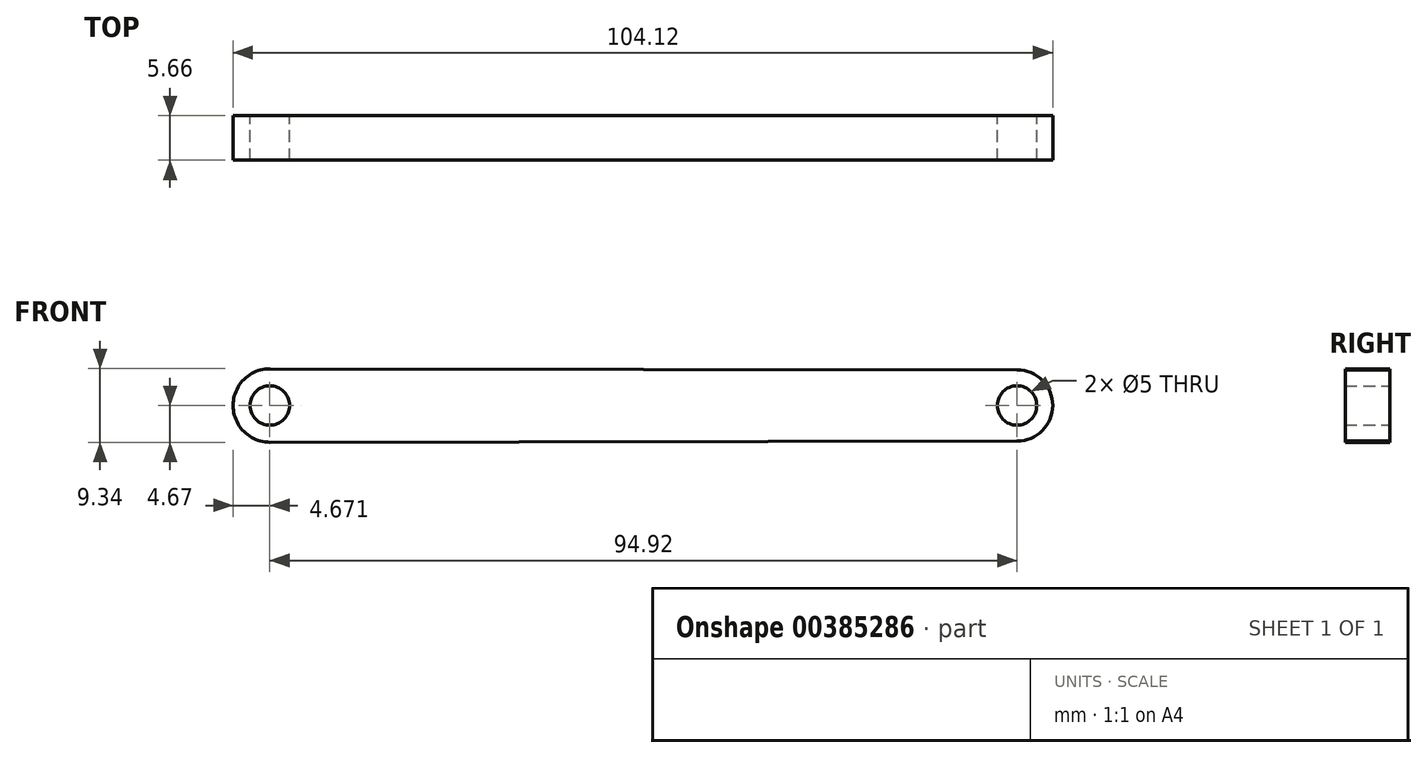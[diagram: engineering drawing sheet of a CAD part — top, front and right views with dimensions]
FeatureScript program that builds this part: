
annotation { "Feature Type Name" : "Feature", "Feature Type Description" : "" }
export const myFeature = defineFeature(function(context is Context, id is Id, definition is map)
    precondition{}
    {
        {
            var Q0;
            Q0=qCreatedBy(makeId("Front.planeOp"),FACE);
            var sketch = newSketch(context, id + "F0", { "sketchPlane" : qUnion([Q0])});
            skCircle(sketch, "E0", {"center": v(-13.37, 0) * mm, "radius": 2.5 * mm});
            skCircle(sketch, "E1", {"center": v(81.55, 0) * mm, "radius": 2.5 * mm});
            skCircle(sketch, "E2", {"center": v(-13.37, 0) * mm, "radius": 4.67 * mm});
            skCircle(sketch, "E3", {"center": v(81.55, 0) * mm, "radius": 4.53 * mm});
            skLineSegment(sketch, "E4", {"start": v(-13.37, 4.67) * mm, "end": v(81.55, 4.53) * mm});
            skLineSegment(sketch, "E5", {"start": v(-13.37, -4.67) * mm, "end": v(81.55, -4.53) * mm});
            skSolve(sketch);
        }
        {
            var Q0;
            Q0 = qSketchRegion(id + "F0", true);
            extrude(context, id + "F1", {"entities" : qUnion([Q0]), "depth" : 5.66 * mm});
        }
    });
